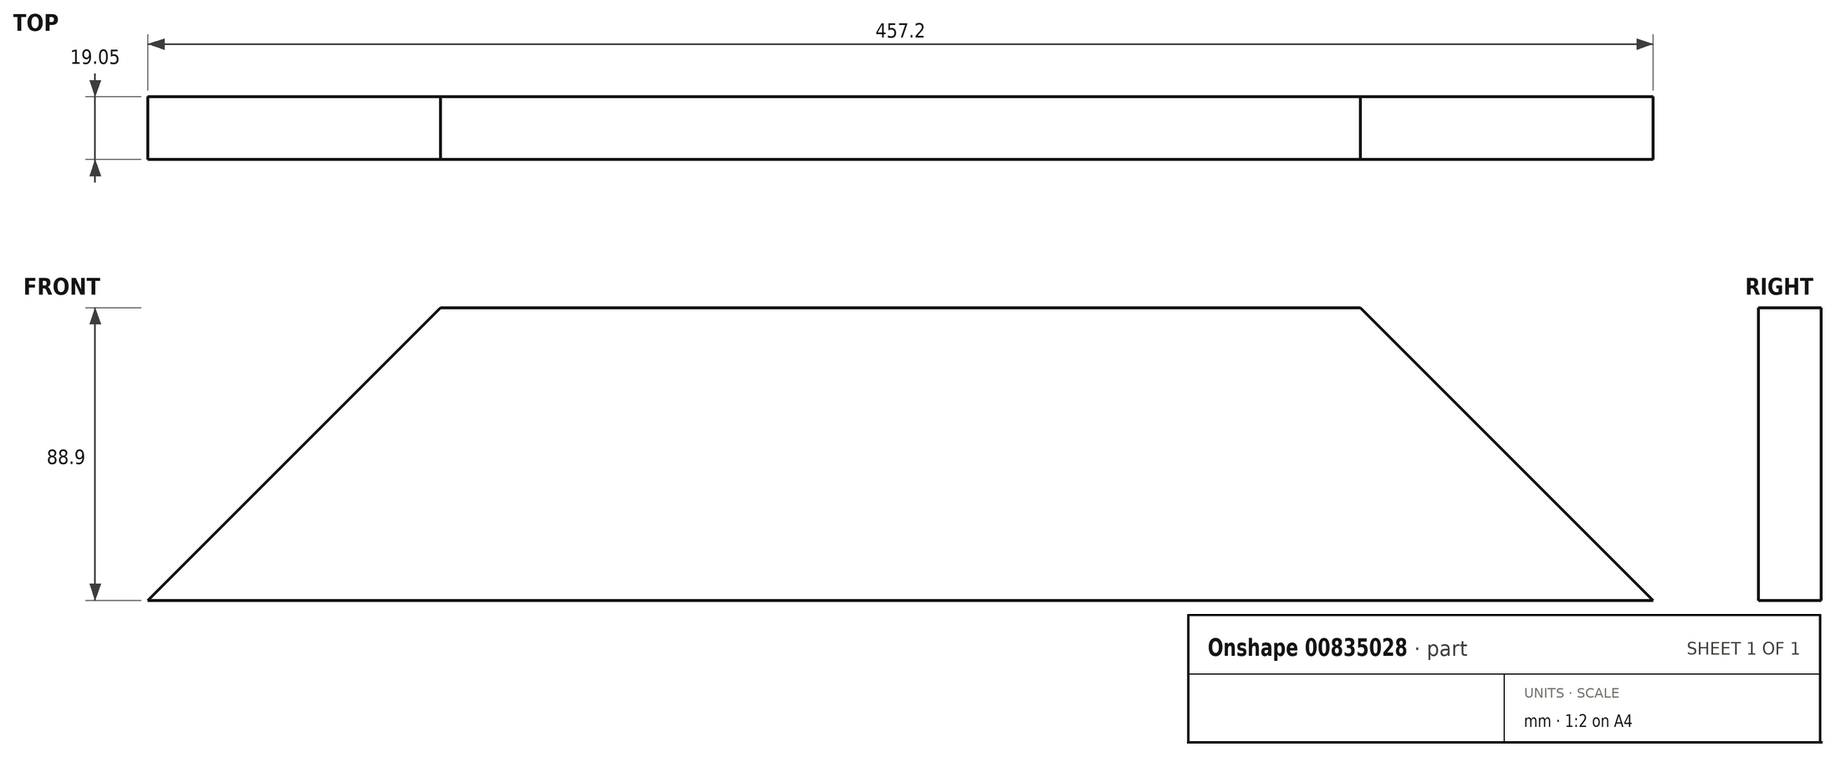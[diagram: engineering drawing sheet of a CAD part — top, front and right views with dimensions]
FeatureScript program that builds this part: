
annotation { "Feature Type Name" : "Feature", "Feature Type Description" : "" }
export const myFeature = defineFeature(function(context is Context, id is Id, definition is map)
    precondition{}
    {
        {
            var Q0;
            Q0=qCreatedBy(makeId("Front.planeOp"),FACE);
            var sketch = newSketch(context, id + "F0", { "sketchPlane" : qUnion([Q0])});
            skLineSegment(sketch, "E0", {"start": v(0, 0) * mm, "end": v(457.2, 0) * mm});
            skLineSegment(sketch, "E1", {"start": v(457.2, 0) * mm, "end": v(368.3, 88.9) * mm});
            skLineSegment(sketch, "E2", {"start": v(368.3, 88.9) * mm, "end": v(88.9, 88.9) * mm});
            skLineSegment(sketch, "E3", {"start": v(88.9, 88.9) * mm, "end": v(0, 0) * mm});
            skSolve(sketch);
        }
        {
            var Q0;
            Q0 = qSketchRegion(id + "F0", true);
            extrude(context, id + "F1", {"entities" : qUnion([Q0]), "depth" : 19.05 * mm, "offsetDistance" : 25.4 * mm});
        }
    });
